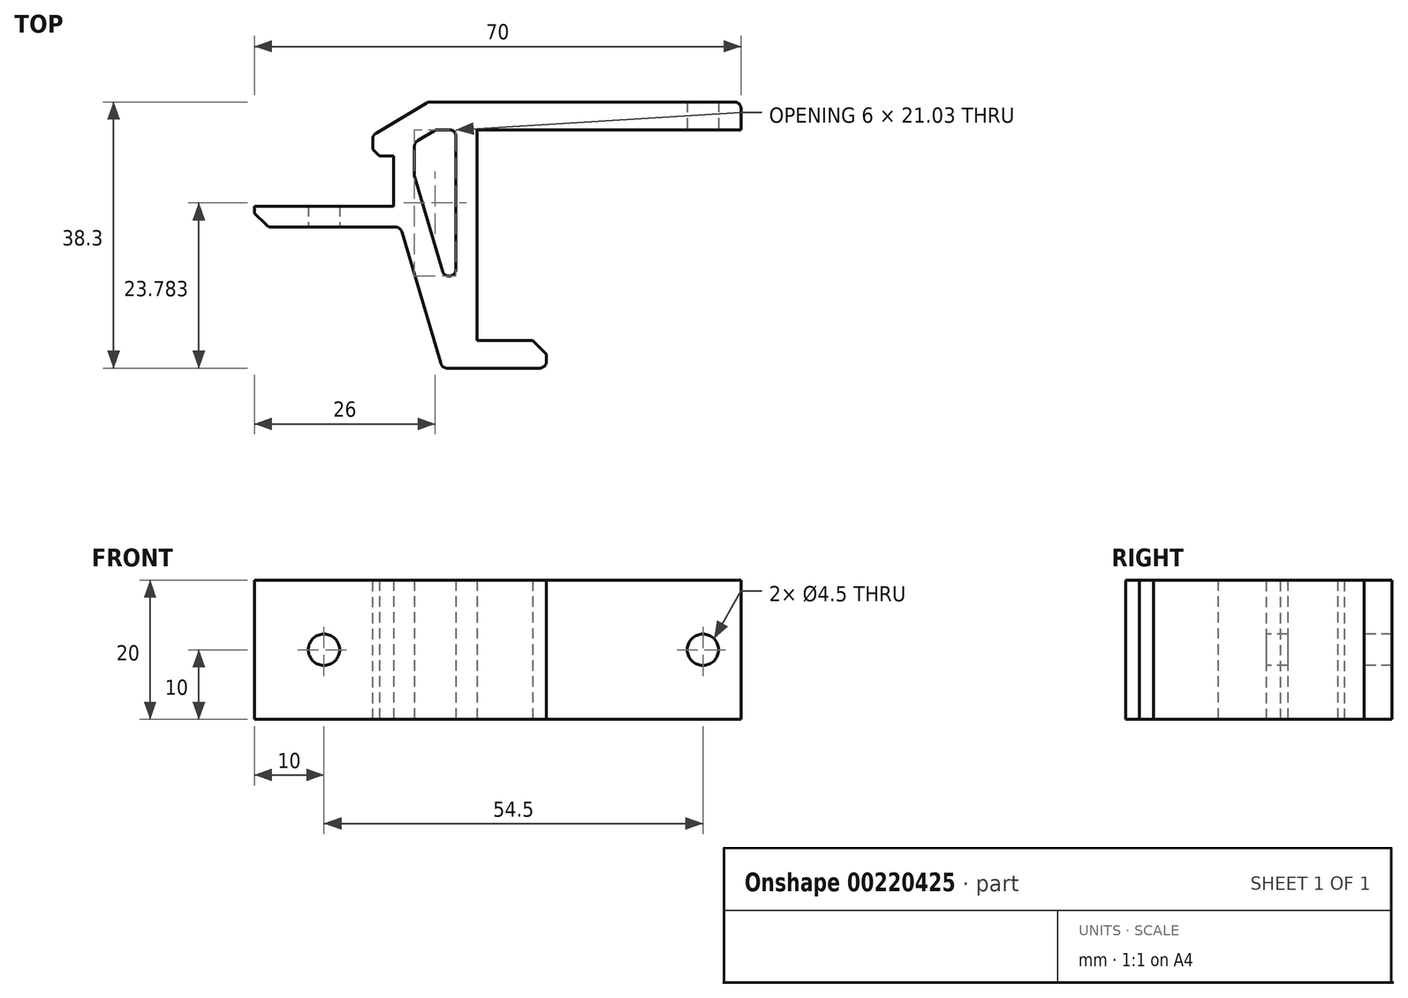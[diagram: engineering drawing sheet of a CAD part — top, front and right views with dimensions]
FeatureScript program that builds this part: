
annotation { "Feature Type Name" : "Feature", "Feature Type Description" : "" }
export const myFeature = defineFeature(function(context is Context, id is Id, definition is map)
    precondition{}
    {
        {
            var Q0;
            Q0=qCreatedBy(makeId("Top.planeOp"),FACE);
            var sketch = newSketch(context, id + "F0", { "sketchPlane" : qUnion([Q0])});
            skPoint(sketch, "E0.0", {"position": v(-10, -10) * mm});
            skPoint(sketch, "E1.0", {"position": v(10, -10) * mm});
            skLineSegment(sketch, "E2", {"start": v(-10, -10) * mm, "end": v(-10, -13) * mm});
            skLineSegment(sketch, "E3", {"start": v(-10, -13) * mm, "end": v(17, -13) * mm, "construction": true});
            skLineSegment(sketch, "E4", {"start": v(17, -13) * mm, "end": v(17, -33.3) * mm, "construction": true});
            skLineSegment(sketch, "E5", {"start": v(17, -33.3) * mm, "end": v(32, -33.3) * mm});
            skLineSegment(sketch, "E6", {"start": v(32, -33.3) * mm, "end": v(32, -29.3) * mm});
            skLineSegment(sketch, "E7", {"start": v(32, -29.3) * mm, "end": v(22, -29.3) * mm});
            skLineSegment(sketch, "E8", {"start": v(22, -29.3) * mm, "end": v(22, 1) * mm});
            skLineSegment(sketch, "E9", {"start": v(22, 1) * mm, "end": v(60, 1) * mm});
            skLineSegment(sketch, "E10", {"start": v(-10, -10) * mm, "end": v(10, -10) * mm});
            skLineSegment(sketch, "E11", {"start": v(10, -2.8) * mm, "end": v(8.5, -2.8) * mm});
            skLineSegment(sketch, "E12", {"start": v(7, -2.8) * mm, "end": v(7, 0.2) * mm});
            skLineSegment(sketch, "E13", {"start": v(15, 5) * mm, "end": v(60, 5) * mm});
            skLineSegment(sketch, "E14", {"start": v(60, 5) * mm, "end": v(60, 1) * mm});
            skLineSegment(sketch, "E15", {"start": v(17, -33.3) * mm, "end": v(11, -13) * mm});
            skLineSegment(sketch, "E16", {"start": v(-10, -13) * mm, "end": v(11, -13) * mm});
            skLineSegment(sketch, "E17", {"start": v(19, 1) * mm, "end": v(19, -25.95) * mm});
            skLineSegment(sketch, "E18", {"start": v(10, -2.8) * mm, "end": v(10, -10) * mm});
            skLineSegment(sketch, "E19", {"start": v(19, 1) * mm, "end": v(16.1, 1) * mm});
            skLineSegment(sketch, "E20", {"start": v(13, -0.86) * mm, "end": v(13, -5.65) * mm});
            skLineSegment(sketch, "E21", {"start": v(13, -5.65) * mm, "end": v(19, -25.95) * mm});
            skLineSegment(sketch, "E22", {"start": v(8.5, -2.8) * mm, "end": v(7, -2.8) * mm});
            skLineSegment(sketch, "E23", {"start": v(7, 0.2) * mm, "end": v(15, 5) * mm});
            skLineSegment(sketch, "E24", {"start": v(16.1, 1) * mm, "end": v(13, -0.86) * mm});
            skLineSegment(sketch, "E25", {"start": v(10, 3) * mm, "end": v(10, -3) * mm, "construction": true});
            skPoint(sketch, "E26", {"position": v(10, 0) * mm});
            skSolve(sketch);
        }
        {
            var Q0;
            Q0=makeQuery(id+"F0.imprint","IMPRINT",FACE,{"disambiguationData":[TD([[makeQuery(id+"F0.imprint","IMPRINT",EDGE,{"derivedFrom":sQuery(id+"F0.wireOp",EDGE,"E2")}),1.0]])]});
            extrude(context, id + "F1", {"entities" : qUnion([Q0]), "depth" : 20 * mm});
        }
        {
            var Q0;
            Q0=makeQuery(id+"F1.opExtrude","SWEPT_FACE",FACE,{"disambiguationData":[OSD([sQuery(id+"F0.wireOp",EDGE,"E9")])]});
            var sketch = newSketch(context, id + "F2", { "sketchPlane" : qUnion([Q0])});
            skLineSegment(sketch, "E27", {"start": v(22, 10) * mm, "end": v(60, 10) * mm, "construction": true});
            skCircle(sketch, "E28", {"center": v(54.5, 10) * mm, "radius": 2.25 * mm});
            skSolve(sketch);
        }
        {
            var Q0;
            Q0=makeQuery(id+"F1.opExtrude","SWEPT_FACE",FACE,{"disambiguationData":[OSD([sQuery(id+"F0.wireOp",EDGE,"E16")])]});
            var sketch = newSketch(context, id + "F3", { "sketchPlane" : qUnion([Q0])});
            skLineSegment(sketch, "E29", {"start": v(0, 20) * mm, "end": v(0, 0) * mm, "construction": true});
            skCircle(sketch, "E30", {"center": v(0, 10) * mm, "radius": 2.25 * mm});
            skSolve(sketch);
        }
        {
            var Q0;
            Q0=makeQuery(id+"F3.imprint","IMPRINT",FACE,{"disambiguationData":[TD([[makeQuery(id+"F3.imprint","IMPRINT",EDGE,{"derivedFrom":sQuery(id+"F3.wireOp",EDGE,"E30")}),1.0]])]});
            var Q1;
            Q1=makeQuery(id+"F2.imprint","IMPRINT",FACE,{"disambiguationData":[TD([[makeQuery(id+"F2.imprint","IMPRINT",EDGE,{"derivedFrom":sQuery(id+"F2.wireOp",EDGE,"E28")}),1.0]])]});
            extrude(context, id + "F4", {"entities" : qUnion([Q0, Q1]), "operationType" : NewBodyOperationType.REMOVE, "endBound" : BoundingType.UP_TO_NEXT, "oppositeDirection" : true, "depth" : 25 * mm});
        }
        {
            var Q0;
            Q0=makeQuery(id+"F1.opExtrude","SWEPT_EDGE",EDGE,{"disambiguationData":[OSD([sQuery(id+"F0.wireOp",EDGE,"E2"),sQuery(id+"F0.wireOp",EDGE,"E16")])]});
            var Q1;
            Q1=makeQuery(id+"F1.opExtrude","SWEPT_EDGE",EDGE,{"disambiguationData":[OSD([sQuery(id+"F0.wireOp",EDGE,"E6"),sQuery(id+"F0.wireOp",EDGE,"E7")])]});
            chamfer(context, id + "F5", {"entities" : qUnion([Q0, Q1]), "width" : 2 * mm, "tangentPropagation" : true});
        }
        {
            var Q0;
            Q0=makeQuery(id+"F1.opExtrude","SWEPT_EDGE",EDGE,{"disambiguationData":[OSD([sQuery(id+"F0.wireOp",EDGE,"E12"),sQuery(id+"F0.wireOp",EDGE,"E23")])]});
            var Q1;
            Q1=makeQuery(id+"F1.opExtrude","SWEPT_EDGE",EDGE,{"disambiguationData":[OSD([sQuery(id+"F0.wireOp",EDGE,"E13"),sQuery(id+"F0.wireOp",EDGE,"E23")])]});
            var Q2;
            Q2=makeQuery(id+"F1.opExtrude","SWEPT_EDGE",EDGE,{"disambiguationData":[OSD([sQuery(id+"F0.wireOp",EDGE,"E13"),sQuery(id+"F0.wireOp",EDGE,"E14")])]});
            var Q3;
            Q3=makeQuery(id+"F1.opExtrude","SWEPT_EDGE",EDGE,{"disambiguationData":[OSD([sQuery(id+"F0.wireOp",EDGE,"E5"),sQuery(id+"F0.wireOp",EDGE,"E15")])]});
            var Q4;
            Q4=makeQuery(id+"F1.opExtrude","SWEPT_EDGE",EDGE,{"disambiguationData":[OSD([sQuery(id+"F0.wireOp",EDGE,"E5"),sQuery(id+"F0.wireOp",EDGE,"E6")])]});
            var Q5;
            Q5=makeQuery(id+"F1.opExtrude","SWEPT_EDGE",EDGE,{"disambiguationData":[OSD([sQuery(id+"F0.wireOp",EDGE,"E17"),sQuery(id+"F0.wireOp",EDGE,"E19")])]});
            var Q6;
            Q6=makeQuery(id+"F1.opExtrude","SWEPT_EDGE",EDGE,{"disambiguationData":[OSD([sQuery(id+"F0.wireOp",EDGE,"E19"),sQuery(id+"F0.wireOp",EDGE,"E24")])]});
            var Q7;
            Q7=makeQuery(id+"F1.opExtrude","SWEPT_EDGE",EDGE,{"disambiguationData":[OSD([sQuery(id+"F0.wireOp",EDGE,"E20"),sQuery(id+"F0.wireOp",EDGE,"E24")])]});
            var Q8;
            Q8=makeQuery(id+"F1.opExtrude","SWEPT_EDGE",EDGE,{"disambiguationData":[OSD([sQuery(id+"F0.wireOp",EDGE,"E20"),sQuery(id+"F0.wireOp",EDGE,"E21")])]});
            var Q9;
            Q9=makeQuery(id+"F1.opExtrude","SWEPT_EDGE",EDGE,{"disambiguationData":[OSD([sQuery(id+"F0.wireOp",EDGE,"E17"),sQuery(id+"F0.wireOp",EDGE,"E19")])]});
            var Q10;
            Q10=makeQuery(id+"F1.opExtrude","SWEPT_EDGE",EDGE,{"disambiguationData":[OSD([sQuery(id+"F0.wireOp",EDGE,"E20"),sQuery(id+"F0.wireOp",EDGE,"E21")])]});
            var Q11;
            Q11=makeQuery(id+"F1.opExtrude","SWEPT_EDGE",EDGE,{"disambiguationData":[OSD([sQuery(id+"F0.wireOp",EDGE,"E17"),sQuery(id+"F0.wireOp",EDGE,"E21")])]});
            var Q12;
            Q12=makeQuery(id+"F1.opExtrude","SWEPT_EDGE",EDGE,{"disambiguationData":[OSD([sQuery(id+"F0.wireOp",EDGE,"E13"),sQuery(id+"F0.wireOp",EDGE,"E14")])]});
            var Q13;
            Q13=makeQuery(id+"F1.opExtrude","SWEPT_EDGE",EDGE,{"disambiguationData":[OSD([sQuery(id+"F0.wireOp",EDGE,"E15"),sQuery(id+"F0.wireOp",EDGE,"E16")])]});
            var Q14;
            {var subQ0=sQuery(id+"F0.wireOp",EDGE,"E16");Q14=makeQuery(id+"F5.opChamfer","BLEND_EDGE",EDGE,{"blendedFrom":[makeQuery(id+"F1.opExtrude","SWEPT_EDGE",EDGE,{"disambiguationData":[OSD([sQuery(id+"F0.wireOp",EDGE,"E2"),subQ0])]}),makeQuery(id+"F1.opExtrude","SWEPT_FACE",FACE,{"disambiguationData":[OSD([subQ0])]})],"blendedInto":[makeQuery(id+"F1.opExtrude","SWEPT_FACE",FACE,{"disambiguationData":[OSD([subQ0])]})]});}
            fillet(context, id + "F6", {"entities" : qUnion([Q0, Q1, Q2, Q3, Q4, Q5, Q6, Q7, Q8, Q9, Q10, Q11, Q12, Q13, Q14]), "radius" : 1 * mm, "tangentPropagation" : true, "allowEdgeOverflow" : false});
        }
        {
            var Q0;
            Q0=makeQuery(id+"F1.opExtrude","SWEPT_EDGE",EDGE,{"disambiguationData":[OSD([sQuery(id+"F0.wireOp",EDGE,"E12"),sQuery(id+"F0.wireOp",EDGE,"E22")])]});
            chamfer(context, id + "F7", {"entities" : qUnion([Q0]), "width" : 1 * mm, "tangentPropagation" : true});
        }
    });
